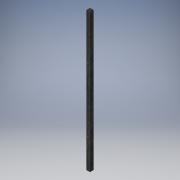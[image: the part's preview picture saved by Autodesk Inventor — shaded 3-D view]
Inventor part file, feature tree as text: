
AUTODESK INVENTOR PART (.ipt)
format: ipt  version: 2019 (Build 230136000, 136)  size: 96,768 bytes
history: native  units: mm
features: extrude x1, sketch x1
ambient origin geometry x8: Origin, YZ Plane, XZ Plane, XY Plane, X Axis, Y Axis, Z Axis, Center Point
bodies: Solid1 (feature_tree)
feature tree (2):
  extrude  "Extrusion1"  Depth=10.0mm
  sketch  "Sketch1"  dims[d0=380.0mm d1=10.0mm d2=10.0mm d3=0.0mm]
